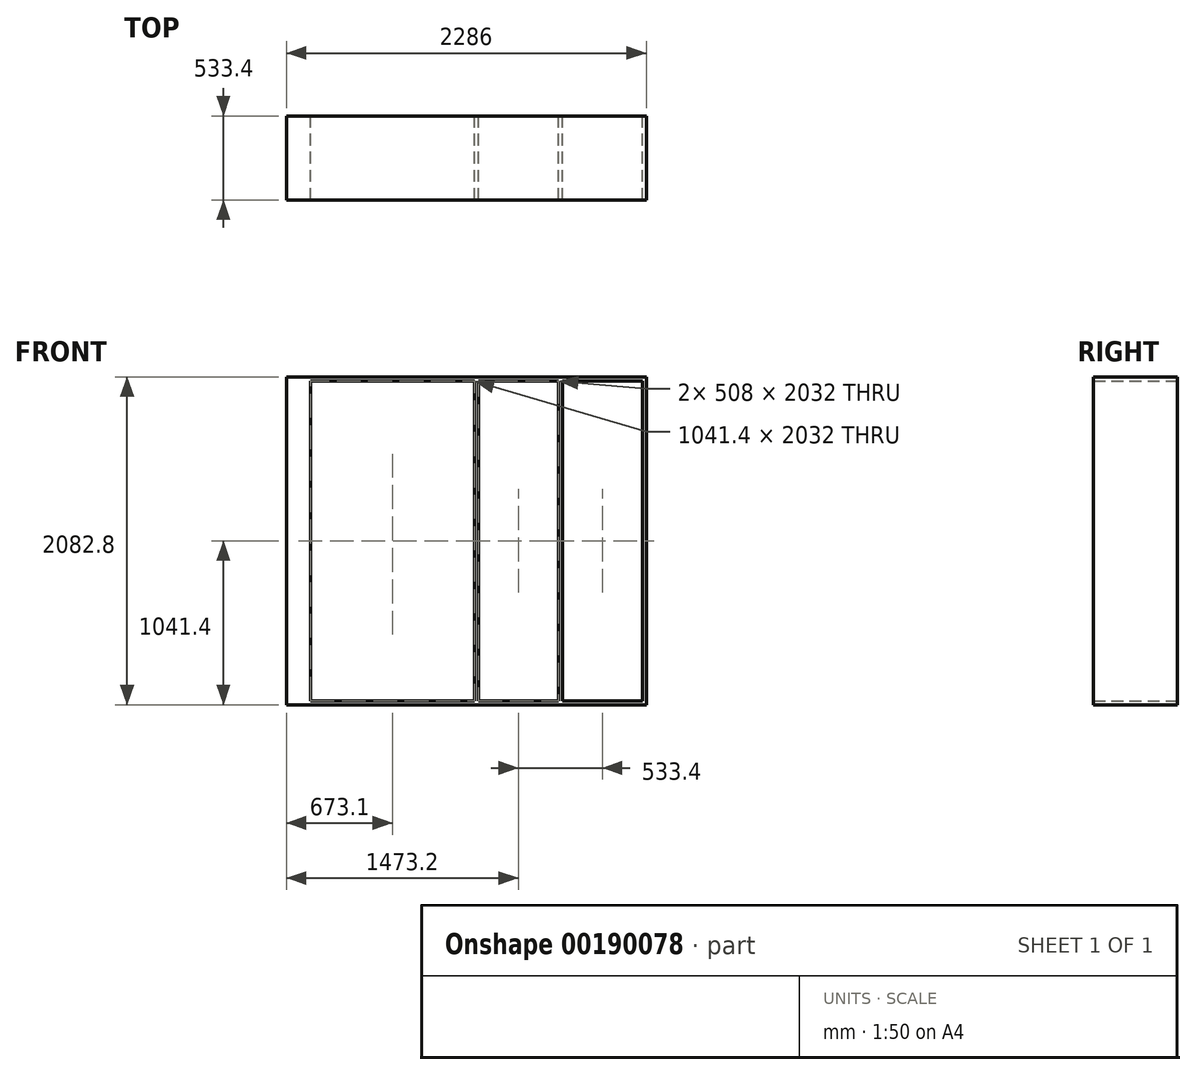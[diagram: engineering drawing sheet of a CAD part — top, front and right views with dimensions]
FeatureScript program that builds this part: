
annotation { "Feature Type Name" : "Feature", "Feature Type Description" : "" }
export const myFeature = defineFeature(function(context is Context, id is Id, definition is map)
    precondition{}
    {
        {
            var Q0;
            Q0=qCreatedBy(makeId("Front.planeOp"),FACE);
            var sketch = newSketch(context, id + "F0", { "sketchPlane" : qUnion([Q0])});
            skLineSegment(sketch, "E0.bottom", {"start": v(1778, -1371.6) * mm, "end": v(-1778, -1371.6) * mm});
            skLineSegment(sketch, "E0.top", {"start": v(1778, 1371.6) * mm, "end": v(-1778, 1371.6) * mm});
            skLineSegment(sketch, "E0.left", {"start": v(1778, -1371.6) * mm, "end": v(1778, 1371.6) * mm});
            skLineSegment(sketch, "E0.right", {"start": v(-1778, -1371.6) * mm, "end": v(-1778, 1371.6) * mm});
            skPoint(sketch, "E0.middle", {"position": v(0, 0) * mm});
            skLineSegment(sketch, "E1.bottom", {"start": v(-1727.2, 762) * mm, "end": v(-508, 762) * mm});
            skLineSegment(sketch, "E1.top", {"start": v(-1727.2, -152.4) * mm, "end": v(-508, -152.4) * mm});
            skLineSegment(sketch, "E1.left", {"start": v(-1727.2, 762) * mm, "end": v(-1727.2, -152.4) * mm});
            skLineSegment(sketch, "E1.right", {"start": v(-508, 762) * mm, "end": v(-508, -152.4) * mm});
            skLineSegment(sketch, "E2.bottom", {"start": v(1778, 711.2) * mm, "end": v(-508, 711.2) * mm});
            skLineSegment(sketch, "E2.top", {"start": v(1778, -1371.6) * mm, "end": v(-508, -1371.6) * mm});
            skLineSegment(sketch, "E2.left", {"start": v(1778, 711.2) * mm, "end": v(1778, -1371.6) * mm});
            skLineSegment(sketch, "E2.right", {"start": v(-508, 711.2) * mm, "end": v(-508, -1371.6) * mm});
            skLineSegment(sketch, "E3.bottom", {"start": v(1752.6, 685.8) * mm, "end": v(1244.6, 685.8) * mm});
            skLineSegment(sketch, "E3.top", {"start": v(1752.6, -1346.2) * mm, "end": v(1244.6, -1346.2) * mm});
            skLineSegment(sketch, "E3.left", {"start": v(1752.6, 685.8) * mm, "end": v(1752.6, -1346.2) * mm});
            skLineSegment(sketch, "E3.right", {"start": v(1244.6, 685.8) * mm, "end": v(1244.6, -1346.2) * mm});
            skLineSegment(sketch, "E4.bottom", {"start": v(1219.2, 685.8) * mm, "end": v(711.2, 685.8) * mm});
            skLineSegment(sketch, "E4.top", {"start": v(1219.2, -1346.2) * mm, "end": v(711.2, -1346.2) * mm});
            skLineSegment(sketch, "E4.left", {"start": v(1219.2, 685.8) * mm, "end": v(1219.2, -1346.2) * mm});
            skLineSegment(sketch, "E4.right", {"start": v(711.2, 685.8) * mm, "end": v(711.2, -1346.2) * mm});
            skLineSegment(sketch, "E5.bottom", {"start": v(-355.6, 685.8) * mm, "end": v(685.8, 685.8) * mm});
            skLineSegment(sketch, "E5.top", {"start": v(-355.6, -1346.2) * mm, "end": v(685.8, -1346.2) * mm});
            skLineSegment(sketch, "E5.left", {"start": v(-355.6, 685.8) * mm, "end": v(-355.6, -1346.2) * mm});
            skLineSegment(sketch, "E5.right", {"start": v(685.8, 685.8) * mm, "end": v(685.8, -1346.2) * mm});
            skSolve(sketch);
        }
        {
            var Q0;
            {var subQ2=sQuery(id+"F0.wireOp",EDGE,"E2.bottom");Q0=makeQuery(id+"F0.imprint","IMPRINT",FACE,{"disambiguationData":[TD([[makeQuery(id+"F0.imprint","IMPRINT",EDGE,{"derivedFrom":subQ2}),1.0]])]});}
            extrude(context, id + "F1", {"entities" : qUnion([Q0]), "depth" : 533.4 * mm});
        }
    });
